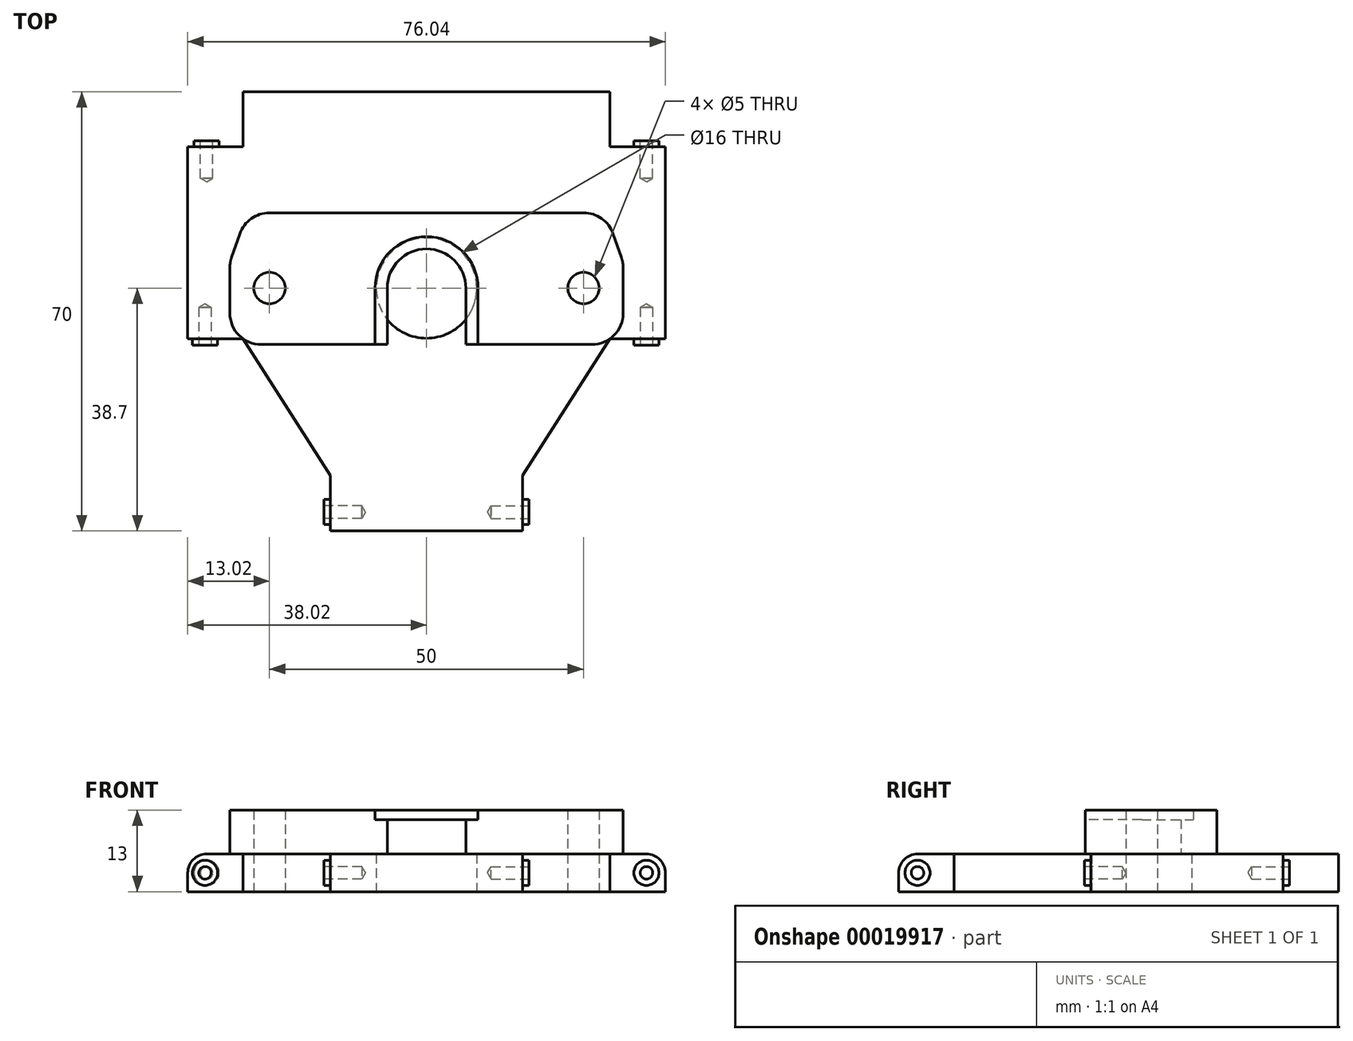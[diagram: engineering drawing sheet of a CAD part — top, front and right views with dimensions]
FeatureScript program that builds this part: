
annotation { "Feature Type Name" : "Feature", "Feature Type Description" : "" }
export const myFeature = defineFeature(function(context is Context, id is Id, definition is map)
    precondition{}
    {
        {
            var Q0;
            Q0=qCreatedBy(makeId("Top.planeOp"),FACE);
            var sketch = newSketch(context, id + "F0", { "sketchPlane" : qUnion([Q0])});
            skCircle(sketch, "E0", {"center": v(0, 0) * mm, "radius": 8 * mm});
            skLineSegment(sketch, "E1", {"start": v(-29.22, 22.5) * mm, "end": v(-38.02, 22.5) * mm});
            skLineSegment(sketch, "E2", {"start": v(-38.02, 22.5) * mm, "end": v(-38.02, -8.1) * mm});
            skLineSegment(sketch, "E3", {"start": v(-38.02, -8.1) * mm, "end": v(-29.22, -8.1) * mm});
            skLineSegment(sketch, "E4", {"start": v(-15.3, -29.9) * mm, "end": v(-15.3, -38.7) * mm});
            skLineSegment(sketch, "E5", {"start": v(-15.3, -38.7) * mm, "end": v(15.3, -38.7) * mm});
            skLineSegment(sketch, "E6", {"start": v(15.3, -38.7) * mm, "end": v(15.3, -29.9) * mm});
            skLineSegment(sketch, "E7", {"start": v(38.02, -8.1) * mm, "end": v(38.02, 22.5) * mm});
            skLineSegment(sketch, "E8", {"start": v(38.02, 22.5) * mm, "end": v(29.22, 22.5) * mm});
            skLineSegment(sketch, "E9", {"start": v(0, 0) * mm, "end": v(0, -38.7) * mm, "construction": true});
            skLineSegment(sketch, "E10", {"start": v(-29.22, -8.1) * mm, "end": v(-15.3, -29.9) * mm});
            skCircle(sketch, "E11", {"center": v(-25, 0) * mm, "radius": 2.5 * mm});
            skCircle(sketch, "E12", {"center": v(25, 0) * mm, "radius": 2.5 * mm});
            skLineSegment(sketch, "E13", {"start": v(38.02, -8.1) * mm, "end": v(29.22, -8.1) * mm});
            skLineSegment(sketch, "E14", {"start": v(29.22, -8.1) * mm, "end": v(15.3, -29.9) * mm});
            skLineSegment(sketch, "E15", {"start": v(0, 0) * mm, "end": v(-38.02, 7.2) * mm, "construction": true});
            skLineSegment(sketch, "E16", {"start": v(0, 0) * mm, "end": v(38.02, 7.2) * mm, "construction": true});
            skLineSegment(sketch, "E17", {"start": v(-29.22, 22.5) * mm, "end": v(-29.22, 31.3) * mm});
            skLineSegment(sketch, "E18", {"start": v(-29.22, 31.3) * mm, "end": v(29.22, 31.3) * mm});
            skLineSegment(sketch, "E19", {"start": v(29.22, 31.3) * mm, "end": v(29.22, 22.5) * mm});
            skSolve(sketch);
        }
        {
            var Q0;
            Q0=qSketchRegion(id+"F0",true);
            extrude(context, id + "F1", {"entities" : qUnion([Q0]), "depth" : 3 * mm, "hasSecondDirection" : true, "secondDirectionOppositeDirection" : true, "secondDirectionDepth" : 3 * mm});
        }
        {
            var Q0;
            Q0=makeQuery(id+"F1.opExtrude","CAP_EDGE",EDGE,{"disambiguationData":[OSD([sQuery(id+"F0.wireOp",EDGE,"E7")])],"isStart":false});
            var Q1;
            Q1=makeQuery(id+"F1.opExtrude","CAP_EDGE",EDGE,{"disambiguationData":[OSD([sQuery(id+"F0.wireOp",EDGE,"E2")])],"isStart":false});
            var Q2;
            Q2=makeQuery(id+"F1.opExtrude","CAP_EDGE",EDGE,{"disambiguationData":[OSD([sQuery(id+"F0.wireOp",EDGE,"E5")])],"isStart":false});
            fillet(context, id + "F2", {"entities" : qUnion([Q0, Q1, Q2]), "radius" : 3 * mm, "tangentPropagation" : true, "allowEdgeOverflow" : false});
        }
        {
            var Q0;
            Q0=makeQuery(id+"F1.opExtrude","SWEPT_FACE",FACE,{"disambiguationData":[OSD([sQuery(id+"F0.wireOp",EDGE,"E4")])]});
            var sketch = newSketch(context, id + "F3", { "sketchPlane" : qUnion([Q0])});
            skCircle(sketch, "E20", {"center": v(35.7, 0) * mm, "radius": 2 * mm});
            skSolve(sketch);
        }
        {
            var Q0;
            Q0=qSketchRegion(id+"F3",true);
            extrude(context, id + "F4", {"entities" : qUnion([Q0]), "depth" : 1 * mm});
        }
        {
            var Q0;
            Q0=makeQuery(id+"F4.opExtrude","CAP_FACE",FACE,{"disambiguationData":[OSD([sQuery(id+"F3.wireOp",EDGE,"E20")])],"isStart":false});
            var sketch = newSketch(context, id + "F5", { "sketchPlane" : qUnion([Q0])});
            skPoint(sketch, "E21", {"position": v(35.7, 0) * mm});
            skSolve(sketch);
        }
        {
            var Q0;
            Q0=makeQuery(id+"F4.opExtrude","SWEPT_BODY",BODY,{"disambiguationData":[OSD([sQuery(id+"F3.wireOp",EDGE,"E20")])]});
            var Q1;
            Q1=qCreatedBy(makeId("Right.planeOp"),FACE);
            mirror(context, id + "F6", {"operationType" : NewBodyOperationType.ADD, "entities" : qUnion([Q0]), "mirrorPlane" : qUnion([Q1])});
        }
        {
            var Q0;
            Q0=makeQuery(id+"F1.opExtrude","SWEPT_FACE",FACE,{"disambiguationData":[OSD([sQuery(id+"F0.wireOp",EDGE,"E3")])]});
            var sketch = newSketch(context, id + "F7", { "sketchPlane" : qUnion([Q0])});
            skCircle(sketch, "E22", {"center": v(-35.27, 0) * mm, "radius": 2 * mm});
            skSolve(sketch);
        }
        {
            var Q0;
            Q0=makeQuery(id+"F1.opExtrude","SWEPT_FACE",FACE,{"disambiguationData":[OSD([sQuery(id+"F0.wireOp",EDGE,"E1")])]});
            var sketch = newSketch(context, id + "F8", { "sketchPlane" : qUnion([Q0])});
            skCircle(sketch, "E23", {"center": v(35.02, 0) * mm, "radius": 2 * mm});
            skSolve(sketch);
        }
        {
            var Q0;
            Q0=makeQuery(id+"F1.opExtrude","SWEPT_FACE",FACE,{"disambiguationData":[OSD([sQuery(id+"F0.wireOp",EDGE,"E8")])]});
            var sketch = newSketch(context, id + "F9", { "sketchPlane" : qUnion([Q0])});
            skCircle(sketch, "E24", {"center": v(-35.02, 0) * mm, "radius": 2 * mm});
            skSolve(sketch);
        }
        {
            var Q0;
            Q0=makeQuery(id+"F1.opExtrude","SWEPT_FACE",FACE,{"disambiguationData":[OSD([sQuery(id+"F0.wireOp",EDGE,"E13")])]});
            var sketch = newSketch(context, id + "F10", { "sketchPlane" : qUnion([Q0])});
            skCircle(sketch, "E25", {"center": v(35.02, 0) * mm, "radius": 2 * mm});
            skSolve(sketch);
        }
        {
            var Q0;
            Q0 = qSketchRegion(id + "F7", true);
            var Q1;
            Q1 = qSketchRegion(id + "F10", true);
            extrude(context, id + "F11", {"entities" : qUnion([Q0, Q1]), "operationType" : NewBodyOperationType.ADD, "depth" : 1 * mm});
        }
        {
            var Q0;
            Q0 = qSketchRegion(id + "F8", true);
            var Q1;
            Q1 = qSketchRegion(id + "F9", true);
            extrude(context, id + "F12", {"entities" : qUnion([Q0, Q1]), "operationType" : NewBodyOperationType.ADD, "depth" : 1 * mm});
        }
        {
            var Q0;
            Q0=makeQuery(id+"F11.opExtrude","CAP_FACE",FACE,{"disambiguationData":[OSD([sQuery(id+"F10.wireOp",EDGE,"E25")])],"isStart":false});
            var sketch = newSketch(context, id + "F13", { "sketchPlane" : qUnion([Q0])});
            skPoint(sketch, "E26", {"position": v(35.02, 0) * mm});
            skSolve(sketch);
        }
        {
            var Q0;
            Q0=makeQuery(id+"F11.opExtrude","CAP_FACE",FACE,{"disambiguationData":[OSD([sQuery(id+"F7.wireOp",EDGE,"E22")])],"isStart":false});
            var sketch = newSketch(context, id + "F14", { "sketchPlane" : qUnion([Q0])});
            skPoint(sketch, "E27", {"position": v(-35.27, 0) * mm});
            skSolve(sketch);
        }
        {
            var Q0;
            Q0=makeQuery(id+"F12.opExtrude","CAP_FACE",FACE,{"disambiguationData":[OSD([sQuery(id+"F9.wireOp",EDGE,"E24")])],"isStart":false});
            var sketch = newSketch(context, id + "F15", { "sketchPlane" : qUnion([Q0])});
            skPoint(sketch, "E28", {"position": v(-35.02, 0) * mm});
            skSolve(sketch);
        }
        {
            var Q0;
            Q0=makeQuery(id+"F6.opPattern","COPY",FACE,{"derivedFrom":makeQuery(id+"F4.opExtrude","CAP_FACE",FACE,{"disambiguationData":[OSD([sQuery(id+"F3.wireOp",EDGE,"E20")])],"isStart":false}),"instanceName":"1"});
            var sketch = newSketch(context, id + "F16", { "sketchPlane" : qUnion([Q0])});
            skPoint(sketch, "E29", {"position": v(-35.7, 0) * mm});
            skSolve(sketch);
        }
        {
            var Q0;
            Q0=makeQuery(id+"F12.opExtrude","CAP_FACE",FACE,{"disambiguationData":[OSD([sQuery(id+"F8.wireOp",EDGE,"E23")])],"isStart":false});
            var sketch = newSketch(context, id + "F17", { "sketchPlane" : qUnion([Q0])});
            skPoint(sketch, "E30", {"position": v(35.02, 0) * mm});
            skPoint(sketch, "E31", {"position": v(-35.02, 0) * mm});
            skSolve(sketch);
        }
        {
            var Q0;
            Q0=sQuery(id+"F14.wireOp",VERTEX,"E27");
            var Q1;
            Q1=sQuery(id+"F5.wireOp",VERTEX,"E21");
            var Q2;
            Q2=sQuery(id+"F13.wireOp",VERTEX,"E26");
            var Q3;
            Q3=sQuery(id+"F15.wireOp",VERTEX,"E28");
            var Q4;
            Q4=sQuery(id+"F17.wireOp",VERTEX,"E31");
            var Q5;
            Q5=sQuery(id+"F17.wireOp",VERTEX,"E30");
            var Q6;
            Q6=sQuery(id+"F16.wireOp",VERTEX,"E29");
            var Q7;
            Q7=makeQuery(id+"F1.opExtrude","SWEPT_BODY",BODY,{"disambiguationData":[OSD([sQuery(id+"F0.wireOp",EDGE,"E0"),sQuery(id+"F0.wireOp",EDGE,"E1"),sQuery(id+"F0.wireOp",EDGE,"E2"),sQuery(id+"F0.wireOp",EDGE,"E3"),sQuery(id+"F0.wireOp",EDGE,"E4"),sQuery(id+"F0.wireOp",EDGE,"E5"),sQuery(id+"F0.wireOp",EDGE,"E6"),sQuery(id+"F0.wireOp",EDGE,"E7"),sQuery(id+"F0.wireOp",EDGE,"E8"),sQuery(id+"F0.wireOp",EDGE,"E10"),sQuery(id+"F0.wireOp",EDGE,"E11"),sQuery(id+"F0.wireOp",EDGE,"E12"),sQuery(id+"F0.wireOp",EDGE,"E13"),sQuery(id+"F0.wireOp",EDGE,"E14"),sQuery(id+"F0.wireOp",EDGE,"E17"),sQuery(id+"F0.wireOp",EDGE,"E18"),sQuery(id+"F0.wireOp",EDGE,"E19")])]});
            var Q8;
            Q8=makeQuery(id+"F4.opExtrude","SWEPT_BODY",BODY,{"disambiguationData":[OSD([sQuery(id+"F3.wireOp",EDGE,"E20")])]});
            var Q9;
            Q9=makeQuery(id+"F6.opPattern","COPY",BODY,{"derivedFrom":makeQuery(id+"F4.opExtrude","SWEPT_BODY",BODY,{"disambiguationData":[OSD([sQuery(id+"F3.wireOp",EDGE,"E20")])]}),"instanceName":"1"});
            hole(context, id + "F18", {"style" : HoleStyle.SIMPLE, "holeDiameter" : 2 * mm, "endStyle" : HoleEndStyle.BLIND, "holeDepth" : 6 * mm, "locations" : qUnion([Q0, Q1, Q2, Q3, Q4, Q5, Q6]), "scope" : qUnion([Q7, Q8, Q9])});
        }
        {
            var Q0;
            Q0=makeQuery(id+"F1.opExtrude","CAP_FACE",FACE,{"disambiguationData":[OSD([sQuery(id+"F0.wireOp",EDGE,"E0"),sQuery(id+"F0.wireOp",EDGE,"E1"),sQuery(id+"F0.wireOp",EDGE,"E2"),sQuery(id+"F0.wireOp",EDGE,"E3"),sQuery(id+"F0.wireOp",EDGE,"E4"),sQuery(id+"F0.wireOp",EDGE,"E5"),sQuery(id+"F0.wireOp",EDGE,"E6"),sQuery(id+"F0.wireOp",EDGE,"E7"),sQuery(id+"F0.wireOp",EDGE,"E8"),sQuery(id+"F0.wireOp",EDGE,"E10"),sQuery(id+"F0.wireOp",EDGE,"E11"),sQuery(id+"F0.wireOp",EDGE,"E12"),sQuery(id+"F0.wireOp",EDGE,"E13"),sQuery(id+"F0.wireOp",EDGE,"E14"),sQuery(id+"F0.wireOp",EDGE,"E17"),sQuery(id+"F0.wireOp",EDGE,"E18"),sQuery(id+"F0.wireOp",EDGE,"E19")])],"isStart":false});
            var sketch = newSketch(context, id + "F19", { "sketchPlane" : qUnion([Q0])});
            skCircle(sketch, "E32.0", {"center": v(-25, 0) * mm, "radius": 2.5 * mm});
            skCircle(sketch, "E32.2", {"center": v(25, 0) * mm, "radius": 2.5 * mm});
            skArc(sketch, "E33.1", {"start": v(6.25, 0) * mm, "mid": v(0, 6.25) * mm, "end": v(-6.25, 0) * mm});
            skLineSegment(sketch, "E34", {"start": v(-26.31, -9) * mm, "end": v(-6.25, -9) * mm});
            skLineSegment(sketch, "E35", {"start": v(-31.31, -4) * mm, "end": v(-31.31, 3.22) * mm});
            skLineSegment(sketch, "E36", {"start": v(-31.04, 4.87) * mm, "end": v(-29.72, 8.64) * mm});
            skLineSegment(sketch, "E37", {"start": v(-25, 12) * mm, "end": v(0, 12) * mm});
            skLineSegment(sketch, "E38", {"start": v(0, 12) * mm, "end": v(25, 12) * mm});
            skLineSegment(sketch, "E39", {"start": v(29.72, 8.64) * mm, "end": v(31.04, 4.87) * mm});
            skPoint(sketch, "E40.orphan", {"position": v(-15.3, -29.9) * mm});
            skPoint(sketch, "E41.orphan", {"position": v(15.3, -29.9) * mm});
            skLineSegment(sketch, "E42", {"start": v(31.31, 3.22) * mm, "end": v(31.31, -4) * mm});
            skPoint(sketch, "E43.visualSharp", {"position": v(-31.31, 4.07) * mm});
            skArc(sketch, "E43.filletArc", {"start": v(-31.04, 4.87) * mm, "mid": v(-31.24, 4.06) * mm, "end": v(-31.31, 3.22) * mm});
            skPoint(sketch, "E44.visualSharp", {"position": v(-28.55, 12) * mm});
            skArc(sketch, "E44.filletArc", {"start": v(-25, 12) * mm, "mid": v(-27.9, 11.08) * mm, "end": v(-29.72, 8.64) * mm});
            skPoint(sketch, "E45.visualSharp", {"position": v(28.55, 12) * mm});
            skArc(sketch, "E45.filletArc", {"start": v(29.72, 8.64) * mm, "mid": v(27.9, 11.08) * mm, "end": v(25, 12) * mm});
            skPoint(sketch, "E46.visualSharp", {"position": v(31.31, 4.07) * mm});
            skArc(sketch, "E46.filletArc", {"start": v(31.31, 3.22) * mm, "mid": v(31.24, 4.06) * mm, "end": v(31.04, 4.87) * mm});
            skArc(sketch, "E47.filletArc", {"start": v(26.31, -9) * mm, "mid": v(29.85, -7.54) * mm, "end": v(31.31, -4) * mm});
            skArc(sketch, "E48.filletArc", {"start": v(-31.31, -4) * mm, "mid": v(-29.85, -7.54) * mm, "end": v(-26.31, -9) * mm});
            skLineSegment(sketch, "E49", {"start": v(-6.25, 0) * mm, "end": v(-6.25, -9) * mm});
            skLineSegment(sketch, "E50", {"start": v(6.25, 0) * mm, "end": v(6.25, -9) * mm});
            skLineSegment(sketch, "E51.trimOffspring", {"start": v(6.25, -9) * mm, "end": v(26.31, -9) * mm});
            skSolve(sketch);
        }
        {
            var Q0;
            Q0 = qSketchRegion(id + "F19", true);
            extrude(context, id + "F20", {"entities" : qUnion([Q0]), "depth" : 5.5 * mm});
        }
        {
            var Q0;
            Q0=makeQuery(id+"F20.opExtrude","CAP_FACE",FACE,{"disambiguationData":[OSD([sQuery(id+"F19.wireOp",EDGE,"E32.0"),sQuery(id+"F19.wireOp",EDGE,"E33.1"),sQuery(id+"F19.wireOp",EDGE,"E32.2"),sQuery(id+"F19.wireOp",EDGE,"E34"),sQuery(id+"F19.wireOp",EDGE,"E35"),sQuery(id+"F19.wireOp",EDGE,"E36"),sQuery(id+"F19.wireOp",EDGE,"E37"),sQuery(id+"F19.wireOp",EDGE,"E38"),sQuery(id+"F19.wireOp",EDGE,"E39"),sQuery(id+"F19.wireOp",EDGE,"E42"),sQuery(id+"F19.wireOp",EDGE,"E43.filletArc"),sQuery(id+"F19.wireOp",EDGE,"E44.filletArc"),sQuery(id+"F19.wireOp",EDGE,"E45.filletArc"),sQuery(id+"F19.wireOp",EDGE,"E46.filletArc"),sQuery(id+"F19.wireOp",EDGE,"E47.filletArc"),sQuery(id+"F19.wireOp",EDGE,"E48.filletArc"),sQuery(id+"F19.wireOp",EDGE,"E49"),sQuery(id+"F19.wireOp",EDGE,"E50"),sQuery(id+"F19.wireOp",EDGE,"E51.trimOffspring")])],"isStart":false});
            var sketch = newSketch(context, id + "F21", { "sketchPlane" : qUnion([Q0])});
            skArc(sketch, "E52.0", {"start": v(-31.31, -4) * mm, "mid": v(-29.85, -7.54) * mm, "end": v(-26.31, -9) * mm});
            skLineSegment(sketch, "E52.1", {"start": v(-31.31, -4) * mm, "end": v(-31.31, 3.22) * mm});
            skArc(sketch, "E52.2", {"start": v(-31.04, 4.87) * mm, "mid": v(-31.24, 4.06) * mm, "end": v(-31.31, 3.22) * mm});
            skLineSegment(sketch, "E52.3", {"start": v(-31.04, 4.87) * mm, "end": v(-29.72, 8.64) * mm});
            skArc(sketch, "E52.4", {"start": v(-25, 12) * mm, "mid": v(-27.9, 11.08) * mm, "end": v(-29.72, 8.64) * mm});
            skLineSegment(sketch, "E52.5", {"start": v(-25, 12) * mm, "end": v(25, 12) * mm});
            skArc(sketch, "E52.6", {"start": v(29.72, 8.64) * mm, "mid": v(27.9, 11.08) * mm, "end": v(25, 12) * mm});
            skLineSegment(sketch, "E52.7", {"start": v(29.72, 8.64) * mm, "end": v(31.04, 4.87) * mm});
            skArc(sketch, "E52.8", {"start": v(31.31, 3.22) * mm, "mid": v(31.24, 4.06) * mm, "end": v(31.04, 4.87) * mm});
            skLineSegment(sketch, "E52.9", {"start": v(31.31, 3.22) * mm, "end": v(31.31, -4) * mm});
            skArc(sketch, "E52.10", {"start": v(26.31, -9) * mm, "mid": v(29.85, -7.54) * mm, "end": v(31.31, -4) * mm});
            skArc(sketch, "E53", {"start": v(8.2, 0) * mm, "mid": v(0, 8.2) * mm, "end": v(-8.2, 0) * mm});
            skLineSegment(sketch, "E54", {"start": v(-8.2, 0) * mm, "end": v(-8.2, -9) * mm});
            skLineSegment(sketch, "E55", {"start": v(8.2, 0) * mm, "end": v(8.2, -9) * mm});
            skLineSegment(sketch, "E56", {"start": v(26.31, -9) * mm, "end": v(8.2, -9) * mm});
            skLineSegment(sketch, "E57", {"start": v(-8.2, -9) * mm, "end": v(-26.31, -9) * mm});
            skCircle(sketch, "E58.0", {"center": v(-25, 0) * mm, "radius": 2.5 * mm});
            skCircle(sketch, "E58.1", {"center": v(25, 0) * mm, "radius": 2.5 * mm});
            skSolve(sketch);
        }
        {
            var Q0;
            Q0 = qSketchRegion(id + "F21", true);
            extrude(context, id + "F22", {"entities" : qUnion([Q0]), "operationType" : NewBodyOperationType.ADD, "depth" : 1.5 * mm});
        }
    });
